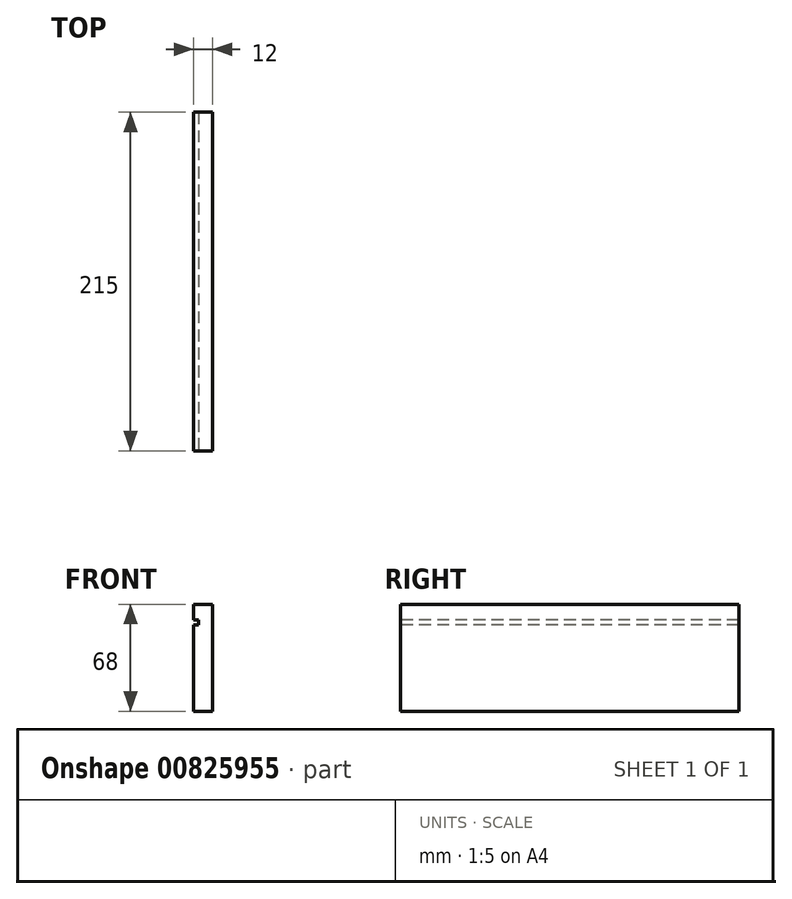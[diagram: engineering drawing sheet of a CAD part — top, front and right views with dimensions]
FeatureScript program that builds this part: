
annotation { "Feature Type Name" : "Feature", "Feature Type Description" : "" }
export const myFeature = defineFeature(function(context is Context, id is Id, definition is map)
    precondition{}
    {
        {
            var Q0;
            Q0=qCreatedBy(makeId("Right.planeOp"),FACE);
            var sketch = newSketch(context, id + "F0", { "sketchPlane" : qUnion([Q0])});
            skLineSegment(sketch, "E0.bottom", {"start": v(-107.5, 34) * mm, "end": v(107.5, 34) * mm});
            skLineSegment(sketch, "E0.top", {"start": v(-107.5, -34) * mm, "end": v(107.5, -34) * mm});
            skLineSegment(sketch, "E0.left", {"start": v(-107.5, 34) * mm, "end": v(-107.5, -34) * mm});
            skLineSegment(sketch, "E0.right", {"start": v(107.5, 34) * mm, "end": v(107.5, -34) * mm});
            skPoint(sketch, "E0.middle", {"position": v(0, 0) * mm});
            skSolve(sketch);
        }
        {
            var Q0;
            Q0 = qSketchRegion(id + "F0", true);
            extrude(context, id + "F1", {"entities" : qUnion([Q0]), "depth" : 12 * mm, "offsetDistance" : 25.4 * mm});
        }
        {
            var Q0;
            Q0=makeQuery(id+"F1.opExtrude","SWEPT_FACE",FACE,{"disambiguationData":[OSD([sQuery(id+"F0.wireOp",EDGE,"E0.left")])]});
            var sketch = newSketch(context, id + "F2", { "sketchPlane" : qUnion([Q0])});
            skLineSegment(sketch, "E1.bottom", {"start": v(0, 21) * mm, "end": v(3, 21) * mm});
            skLineSegment(sketch, "E1.top", {"start": v(0, 24) * mm, "end": v(3, 24) * mm});
            skLineSegment(sketch, "E1.left", {"start": v(0, 21) * mm, "end": v(0, 24) * mm});
            skLineSegment(sketch, "E1.right", {"start": v(3, 21) * mm, "end": v(3, 24) * mm});
            skSolve(sketch);
        }
        {
            var Q0;
            Q0 = qSketchRegion(id + "F2", true);
            extrude(context, id + "F3", {"entities" : qUnion([Q0]), "operationType" : NewBodyOperationType.ADD, "depth" : 300 * mm, "offsetDistance" : 25.4 * mm});
        }
        {
            var Q0;
            Q0=makeQuery(id+"F1.opExtrude","SWEPT_FACE",FACE,{"disambiguationData":[OSD([sQuery(id+"F0.wireOp",EDGE,"E0.left")])]});
            var sketch = newSketch(context, id + "F4", { "sketchPlane" : qUnion([Q0])});
            skSolve(sketch);
        }
        {
            var Q0;
            Q0 = qSketchRegion(id + "F4", true);
            var Q1;
            Q1=makeQuery(id+"F3.opExtrude","CAP_FACE",FACE,{"disambiguationData":[OSD([sQuery(id+"F2.wireOp",EDGE,"E1.bottom"),sQuery(id+"F2.wireOp",EDGE,"E1.top"),sQuery(id+"F2.wireOp",EDGE,"E1.left"),sQuery(id+"F2.wireOp",EDGE,"E1.right")])],"isStart":false});
            extrude(context, id + "F5", {"entities" : qUnion([Q0, Q1]), "operationType" : NewBodyOperationType.REMOVE, "oppositeDirection" : true, "depth" : 800 * mm, "offsetDistance" : 25.4 * mm});
        }
    });
